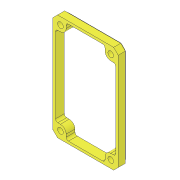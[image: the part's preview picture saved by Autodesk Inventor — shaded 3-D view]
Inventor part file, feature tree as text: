
AUTODESK INVENTOR PART (.ipt)
format: ipt  version: 2019.4 (Build 234330000, 330)  size: 214,528 bytes
history: native  units: mm
features: sketch x2, extrude x2, other x1, hole x1
ambient origin geometry x8: Origin, YZ Plane, XZ Plane, XY Plane, X Axis, Y Axis, Z Axis, Center Point
bodies: Body1 (feature_tree)
feature tree (6):
  other  "ソリッド1"
  sketch  "スケッチ1"
  extrude  "押し出し1"  Depth=2.0mm
  hole  "穴1"  [1 undecoded]
  extrude  "押し出し2"  Depth=2.0mm
  sketch  "スケッチ3"
note: 1 required parameter value undecoded (feature->parameter linkage not recoverable at this tier; creation-order binding heuristic only, values carry confidence <= 0.55)
